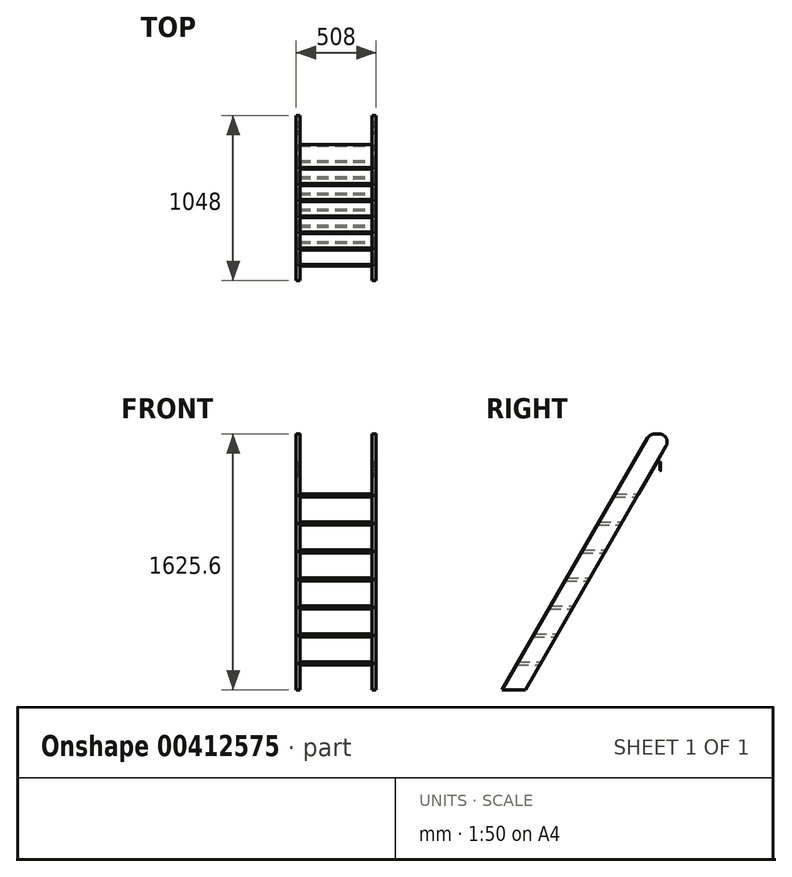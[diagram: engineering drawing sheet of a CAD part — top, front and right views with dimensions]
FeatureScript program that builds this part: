
annotation { "Feature Type Name" : "Feature", "Feature Type Description" : "" }
export const myFeature = defineFeature(function(context is Context, id is Id, definition is map)
    precondition{}
    {
        {
            var Q0;
            Q0=qCreatedBy(makeId("Right.planeOp"),FACE);
            var sketch = newSketch(context, id + "F0", { "sketchPlane" : qUnion([Q0])});
            skLineSegment(sketch, "E0", {"start": v(-87.99, 0) * mm, "end": v(-117.32, 0) * mm});
            skLineSegment(sketch, "E1", {"start": v(-161.31, -25.4) * mm, "end": v(-1085.19, -1625.6) * mm});
            skLineSegment(sketch, "E2", {"start": v(-1085.19, -1625.6) * mm, "end": v(-938.54, -1625.6) * mm});
            skLineSegment(sketch, "E3", {"start": v(-938.54, -1625.6) * mm, "end": v(-154.37, -267.38) * mm});
            skLineSegment(sketch, "E4", {"start": v(-982.53, -1447.8) * mm, "end": v(-835.89, -1447.8) * mm});
            skLineSegment(sketch, "E5", {"start": v(-879.88, -1270) * mm, "end": v(-733.23, -1270) * mm});
            skLineSegment(sketch, "E6", {"start": v(-777.23, -1092.2) * mm, "end": v(-630.58, -1092.2) * mm});
            skLineSegment(sketch, "E7", {"start": v(-674.58, -914.4) * mm, "end": v(-527.93, -914.4) * mm});
            skLineSegment(sketch, "E8", {"start": v(-571.92, -736.6) * mm, "end": v(-425.28, -736.6) * mm});
            skLineSegment(sketch, "E9.0", {"start": v(-993.53, -1466.85) * mm, "end": v(-846.89, -1466.85) * mm});
            skLineSegment(sketch, "E10.0", {"start": v(-890.88, -1289.05) * mm, "end": v(-744.23, -1289.05) * mm});
            skLineSegment(sketch, "E11.0", {"start": v(-788.23, -1111.25) * mm, "end": v(-641.58, -1111.25) * mm});
            skLineSegment(sketch, "E12.0", {"start": v(-685.57, -933.45) * mm, "end": v(-538.93, -933.45) * mm});
            skLineSegment(sketch, "E13.0", {"start": v(-582.92, -755.65) * mm, "end": v(-436.27, -755.65) * mm});
            skLineSegment(sketch, "E14.0", {"start": v(-469.27, -558.8) * mm, "end": v(-322.62, -558.8) * mm});
            skLineSegment(sketch, "E15.0", {"start": v(-480.27, -577.85) * mm, "end": v(-333.62, -577.85) * mm});
            skLineSegment(sketch, "E16.0", {"start": v(-366.62, -381) * mm, "end": v(-219.97, -381) * mm});
            skLineSegment(sketch, "E17.0", {"start": v(-377.62, -400.05) * mm, "end": v(-230.97, -400.05) * mm});
            skArc(sketch, "E18.filletArc", {"start": v(-117.32, 0) * mm, "mid": v(-142.72, -6.8) * mm, "end": v(-161.31, -25.4) * mm});
            skPoint(sketch, "E19.visualSharp", {"position": v(0, 0) * mm});
            skArc(sketch, "E19.filletArc", {"start": v(-44, -76.2) * mm, "mid": v(-44, -25.4) * mm, "end": v(-87.99, 0) * mm});
            skLineSegment(sketch, "E20", {"start": v(-78.6, -180.98) * mm, "end": v(-78.6, -231.78) * mm});
            skLineSegment(sketch, "E21", {"start": v(-78.6, -231.78) * mm, "end": v(-81.77, -231.78) * mm});
            skLineSegment(sketch, "E22", {"start": v(-81.77, -231.78) * mm, "end": v(-81.77, -184.15) * mm});
            skLineSegment(sketch, "E23", {"start": v(-81.77, -177.8) * mm, "end": v(-102.65, -177.8) * mm});
            skLineSegment(sketch, "E24.trimOffspring", {"start": v(-154.37, -267.38) * mm, "end": v(-44, -76.2) * mm});
            skLineSegment(sketch, "E25.0", {"start": v(-84.94, -180.98) * mm, "end": v(-100.82, -180.98) * mm});
            skPoint(sketch, "E26.visualSharp", {"position": v(-100.82, -180.98) * mm});
            skPoint(sketch, "E27.visualSharp", {"position": v(-81.77, -180.98) * mm});
            skArc(sketch, "E27.filletArc", {"start": v(-81.77, -184.15) * mm, "mid": v(-82.7, -181.9) * mm, "end": v(-84.94, -180.98) * mm});
            skPoint(sketch, "E28.visualSharp", {"position": v(-78.6, -177.8) * mm});
            skArc(sketch, "E28.filletArc", {"start": v(-78.6, -180.98) * mm, "mid": v(-79.52, -178.73) * mm, "end": v(-81.77, -177.8) * mm});
            skPoint(sketch, "E29.visualSharp", {"position": v(-102.65, -177.8) * mm});
            skLineSegment(sketch, "E30", {"start": v(-102.65, -177.8) * mm, "end": v(-154.37, -267.38) * mm});
            skLineSegment(sketch, "E31", {"start": v(-154.37, -267.38) * mm, "end": v(-151.62, -268.96) * mm});
            skLineSegment(sketch, "E32", {"start": v(-151.62, -268.96) * mm, "end": v(-100.82, -180.98) * mm});
            skSolve(sketch);
        }
        {
            var Q0;
            Q0=makeQuery(id+"F0.imprint","IMPRINT",FACE,{"disambiguationData":[TD([[makeQuery(id+"F0.imprint","IMPRINT",EDGE,{"derivedFrom":sQuery(id+"F0.wireOp",EDGE,"E0")}),1.0]])]});
            var Q1;
            {var subQ0=sQuery(id+"F0.wireOp",EDGE,"E16.0");Q1=makeQuery(id+"F0.imprint","IMPRINT",FACE,{"disambiguationData":[TD([[makeQuery(id+"F0.imprint","IMPRINT",EDGE,{"derivedFrom":subQ0}),-1.0]])]});}
            var Q2;
            {var subQ0=sQuery(id+"F0.wireOp",EDGE,"E14.0");Q2=makeQuery(id+"F0.imprint","IMPRINT",FACE,{"disambiguationData":[TD([[makeQuery(id+"F0.imprint","IMPRINT",EDGE,{"derivedFrom":subQ0}),1.0]])]});}
            var Q3;
            {var subQ0=sQuery(id+"F0.wireOp",EDGE,"E14.0");Q3=makeQuery(id+"F0.imprint","IMPRINT",FACE,{"disambiguationData":[TD([[makeQuery(id+"F0.imprint","IMPRINT",EDGE,{"derivedFrom":subQ0}),-1.0]])]});}
            var Q4;
            {var subQ0=sQuery(id+"F0.wireOp",EDGE,"E8");Q4=makeQuery(id+"F0.imprint","IMPRINT",FACE,{"disambiguationData":[TD([[makeQuery(id+"F0.imprint","IMPRINT",EDGE,{"derivedFrom":subQ0}),1.0]])]});}
            var Q5;
            {var subQ0=sQuery(id+"F0.wireOp",EDGE,"E8");Q5=makeQuery(id+"F0.imprint","IMPRINT",FACE,{"disambiguationData":[TD([[makeQuery(id+"F0.imprint","IMPRINT",EDGE,{"derivedFrom":subQ0}),-1.0]])]});}
            var Q6;
            {var subQ0=sQuery(id+"F0.wireOp",EDGE,"E7");Q6=makeQuery(id+"F0.imprint","IMPRINT",FACE,{"disambiguationData":[TD([[makeQuery(id+"F0.imprint","IMPRINT",EDGE,{"derivedFrom":subQ0}),1.0]])]});}
            var Q7;
            {var subQ0=sQuery(id+"F0.wireOp",EDGE,"E6");Q7=makeQuery(id+"F0.imprint","IMPRINT",FACE,{"disambiguationData":[TD([[makeQuery(id+"F0.imprint","IMPRINT",EDGE,{"derivedFrom":subQ0}),1.0]])]});}
            var Q8;
            {var subQ0=sQuery(id+"F0.wireOp",EDGE,"E5");Q8=makeQuery(id+"F0.imprint","IMPRINT",FACE,{"disambiguationData":[TD([[makeQuery(id+"F0.imprint","IMPRINT",EDGE,{"derivedFrom":subQ0}),1.0]])]});}
            var Q9;
            {var subQ0=sQuery(id+"F0.wireOp",EDGE,"E4");Q9=makeQuery(id+"F0.imprint","IMPRINT",FACE,{"disambiguationData":[TD([[makeQuery(id+"F0.imprint","IMPRINT",EDGE,{"derivedFrom":subQ0}),1.0]])]});}
            var Q10;
            {var subQ0=sQuery(id+"F0.wireOp",EDGE,"E2");Q10=makeQuery(id+"F0.imprint","IMPRINT",FACE,{"disambiguationData":[TD([[makeQuery(id+"F0.imprint","IMPRINT",EDGE,{"derivedFrom":subQ0}),1.0]])]});}
            var Q11;
            {var subQ0=sQuery(id+"F0.wireOp",EDGE,"E4");Q11=makeQuery(id+"F0.imprint","IMPRINT",FACE,{"disambiguationData":[TD([[makeQuery(id+"F0.imprint","IMPRINT",EDGE,{"derivedFrom":subQ0}),-1.0]])]});}
            var Q12;
            {var subQ0=sQuery(id+"F0.wireOp",EDGE,"E5");Q12=makeQuery(id+"F0.imprint","IMPRINT",FACE,{"disambiguationData":[TD([[makeQuery(id+"F0.imprint","IMPRINT",EDGE,{"derivedFrom":subQ0}),-1.0]])]});}
            var Q13;
            {var subQ0=sQuery(id+"F0.wireOp",EDGE,"E6");Q13=makeQuery(id+"F0.imprint","IMPRINT",FACE,{"disambiguationData":[TD([[makeQuery(id+"F0.imprint","IMPRINT",EDGE,{"derivedFrom":subQ0}),-1.0]])]});}
            var Q14;
            {var subQ0=sQuery(id+"F0.wireOp",EDGE,"E7");Q14=makeQuery(id+"F0.imprint","IMPRINT",FACE,{"disambiguationData":[TD([[makeQuery(id+"F0.imprint","IMPRINT",EDGE,{"derivedFrom":subQ0}),-1.0]])]});}
            var Q15;
            {var subQ0=sQuery(id+"F0.wireOp",EDGE,"B96Wzpzp-lwjt-oDgw-DfDW-PDG2NPqT7k9v");Q15=makeQuery(id+"F0.imprint","IMPRINT",FACE,{"disambiguationData":[TD([[makeQuery(id+"F0.imprint","IMPRINT",EDGE,{"derivedFrom":subQ0}),-1.0]])]});}
            extrude(context, id + "F1", {"entities" : qUnion([Q0, Q1, Q2, Q3, Q4, Q5, Q6, Q7, Q8, Q9, Q10, Q11, Q12, Q13, Q14, Q15]), "depth" : 25.4 * mm});
        }
        {
            var Q0;
            {var subQ0=sQuery(id+"F0.wireOp",EDGE,"E16.0");Q0=makeQuery(id+"F0.imprint","IMPRINT",FACE,{"disambiguationData":[TD([[makeQuery(id+"F0.imprint","IMPRINT",EDGE,{"derivedFrom":subQ0}),-1.0]])]});}
            var Q1;
            {var subQ0=sQuery(id+"F0.wireOp",EDGE,"E14.0");Q1=makeQuery(id+"F0.imprint","IMPRINT",FACE,{"disambiguationData":[TD([[makeQuery(id+"F0.imprint","IMPRINT",EDGE,{"derivedFrom":subQ0}),-1.0]])]});}
            var Q2;
            {var subQ0=sQuery(id+"F0.wireOp",EDGE,"E8");Q2=makeQuery(id+"F0.imprint","IMPRINT",FACE,{"disambiguationData":[TD([[makeQuery(id+"F0.imprint","IMPRINT",EDGE,{"derivedFrom":subQ0}),-1.0]])]});}
            var Q3;
            {var subQ0=sQuery(id+"F0.wireOp",EDGE,"E7");Q3=makeQuery(id+"F0.imprint","IMPRINT",FACE,{"disambiguationData":[TD([[makeQuery(id+"F0.imprint","IMPRINT",EDGE,{"derivedFrom":subQ0}),-1.0]])]});}
            var Q4;
            {var subQ0=sQuery(id+"F0.wireOp",EDGE,"E6");Q4=makeQuery(id+"F0.imprint","IMPRINT",FACE,{"disambiguationData":[TD([[makeQuery(id+"F0.imprint","IMPRINT",EDGE,{"derivedFrom":subQ0}),-1.0]])]});}
            var Q5;
            {var subQ0=sQuery(id+"F0.wireOp",EDGE,"E5");Q5=makeQuery(id+"F0.imprint","IMPRINT",FACE,{"disambiguationData":[TD([[makeQuery(id+"F0.imprint","IMPRINT",EDGE,{"derivedFrom":subQ0}),-1.0]])]});}
            var Q6;
            {var subQ0=sQuery(id+"F0.wireOp",EDGE,"E4");Q6=makeQuery(id+"F0.imprint","IMPRINT",FACE,{"disambiguationData":[TD([[makeQuery(id+"F0.imprint","IMPRINT",EDGE,{"derivedFrom":subQ0}),-1.0]])]});}
            extrude(context, id + "F2", {"entities" : qUnion([Q0, Q1, Q2, Q3, Q4, Q5, Q6]), "operationType" : NewBodyOperationType.REMOVE, "depth" : 9.52 * mm});
        }
        {
            var Q0;
            Q0=makeQuery(id+"F0.imprint","IMPRINT",FACE,{"disambiguationData":[TD([[makeQuery(id+"F0.imprint","IMPRINT",EDGE,{"derivedFrom":sQuery(id+"F0.wireOp",EDGE,"E20")}),-1.0]])]});
            extrude(context, id + "F3", {"entities" : qUnion([Q0]), "depth" : 25.4 * mm});
        }
        {
            var Q0;
            Q0=qCreatedBy(makeId("Right.planeOp"),FACE);
            cPlane(context, id + "F4", {"entities" : qUnion([Q0]), "cplaneType" : CPlaneType.OFFSET, "offset" : 228.6 * mm, "oppositeDirection" : true, "width" : 152.4 * mm, "height" : 152.4 * mm});
        }
        {
            var Q0;
            Q0=makeQuery(id+"F1.opExtrude","SWEPT_BODY",BODY,{"disambiguationData":[OSD([sQuery(id+"F0.wireOp",EDGE,"E0"),sQuery(id+"F0.wireOp",EDGE,"E1"),sQuery(id+"F0.wireOp",EDGE,"E2"),sQuery(id+"F0.wireOp",EDGE,"E3"),sQuery(id+"F0.wireOp",EDGE,"E18.filletArc"),sQuery(id+"F0.wireOp",EDGE,"E19.filletArc"),sQuery(id+"F0.wireOp",EDGE,"87bb9fc3-04ee-44ed-8673-97e675bece17.0"),sQuery(id+"F0.wireOp",EDGE,"B96Wzpzp-lwjt-oDgw-DfDW-PDG2NPqT7k9v"),sQuery(id+"F0.wireOp",EDGE,"E24.trimOffspring")])]});
            var Q1;
            Q1=qCreatedBy(id+"F4.planeOp",FACE);
            mirror(context, id + "F5", {"entities" : qUnion([Q0]), "mirrorPlane" : qUnion([Q1])});
        }
        {
            var Q0;
            Q0=makeQuery(id+"F2.boolean.opBoolean","COPY",FACE,{"derivedFrom":makeQuery(id+"F2.opExtrude","CAP_FACE",FACE,{"disambiguationData":[OSD([sQuery(id+"F0.wireOp",EDGE,"E1"),sQuery(id+"F0.wireOp",EDGE,"E3"),sQuery(id+"F0.wireOp",EDGE,"E16.0"),sQuery(id+"F0.wireOp",EDGE,"E17.0")])],"isStart":false})});
            var Q1;
            Q1=makeQuery(id+"F2.boolean.opBoolean","COPY",FACE,{"derivedFrom":makeQuery(id+"F2.opExtrude","CAP_FACE",FACE,{"disambiguationData":[OSD([sQuery(id+"F0.wireOp",EDGE,"E1"),sQuery(id+"F0.wireOp",EDGE,"E3"),sQuery(id+"F0.wireOp",EDGE,"E14.0"),sQuery(id+"F0.wireOp",EDGE,"E15.0")])],"isStart":false})});
            var Q2;
            Q2=makeQuery(id+"F2.boolean.opBoolean","COPY",FACE,{"derivedFrom":makeQuery(id+"F2.opExtrude","CAP_FACE",FACE,{"disambiguationData":[OSD([sQuery(id+"F0.wireOp",EDGE,"E1"),sQuery(id+"F0.wireOp",EDGE,"E3"),sQuery(id+"F0.wireOp",EDGE,"E8"),sQuery(id+"F0.wireOp",EDGE,"E13.0")])],"isStart":false})});
            var Q3;
            Q3=makeQuery(id+"F2.boolean.opBoolean","COPY",FACE,{"derivedFrom":makeQuery(id+"F2.opExtrude","CAP_FACE",FACE,{"disambiguationData":[OSD([sQuery(id+"F0.wireOp",EDGE,"E1"),sQuery(id+"F0.wireOp",EDGE,"E3"),sQuery(id+"F0.wireOp",EDGE,"E7"),sQuery(id+"F0.wireOp",EDGE,"E12.0")])],"isStart":false})});
            var Q4;
            Q4=makeQuery(id+"F2.boolean.opBoolean","COPY",FACE,{"derivedFrom":makeQuery(id+"F2.opExtrude","CAP_FACE",FACE,{"disambiguationData":[OSD([sQuery(id+"F0.wireOp",EDGE,"E1"),sQuery(id+"F0.wireOp",EDGE,"E3"),sQuery(id+"F0.wireOp",EDGE,"E6"),sQuery(id+"F0.wireOp",EDGE,"E11.0")])],"isStart":false})});
            var Q5;
            Q5=makeQuery(id+"F2.boolean.opBoolean","COPY",FACE,{"derivedFrom":makeQuery(id+"F2.opExtrude","CAP_FACE",FACE,{"disambiguationData":[OSD([sQuery(id+"F0.wireOp",EDGE,"E1"),sQuery(id+"F0.wireOp",EDGE,"E3"),sQuery(id+"F0.wireOp",EDGE,"E5"),sQuery(id+"F0.wireOp",EDGE,"E10.0")])],"isStart":false})});
            var Q6;
            Q6=makeQuery(id+"F2.boolean.opBoolean","COPY",FACE,{"derivedFrom":makeQuery(id+"F2.opExtrude","CAP_FACE",FACE,{"disambiguationData":[OSD([sQuery(id+"F0.wireOp",EDGE,"E1"),sQuery(id+"F0.wireOp",EDGE,"E3"),sQuery(id+"F0.wireOp",EDGE,"E4"),sQuery(id+"F0.wireOp",EDGE,"E9.0")])],"isStart":false})});
            extrude(context, id + "F6", {"entities" : qUnion([Q0, Q1, Q2, Q3, Q4, Q5, Q6]), "endBound" : BoundingType.UP_TO_NEXT, "depth" : 457.2 * mm});
        }
        {
            var Q0;
            Q0=makeQuery(id+"F3.opExtrude","SWEPT_FACE",FACE,{"disambiguationData":[OSD([sQuery(id+"F0.wireOp",EDGE,"E32")])]});
            var sketch = newSketch(context, id + "F7", { "sketchPlane" : qUnion([Q0])});
            skPoint(sketch, "E33", {"position": v(-12.7, -219.84) * mm});
            skPoint(sketch, "E34", {"position": v(-12.7, -289.69) * mm});
            skSolve(sketch);
        }
        {
            var Q0;
            Q0=sQuery(id+"F7.wireOp",VERTEX,"E33");
            var Q1;
            Q1=sQuery(id+"F7.wireOp",VERTEX,"E34");
            var Q2;
            Q2=makeQuery(id+"F3.opExtrude","SWEPT_BODY",BODY,{"disambiguationData":[OSD([sQuery(id+"F0.wireOp",EDGE,"E20"),sQuery(id+"F0.wireOp",EDGE,"E21"),sQuery(id+"F0.wireOp",EDGE,"E22"),sQuery(id+"F0.wireOp",EDGE,"E23"),sQuery(id+"F0.wireOp",EDGE,"87bb9fc3-04ee-44ed-8673-97e675bece17.0"),sQuery(id+"F0.wireOp",EDGE,"a5deaf5e-a050-4f96-910e-6dbd6f1f3d3d.0"),sQuery(id+"F0.wireOp",EDGE,"E25.0"),sQuery(id+"F0.wireOp",EDGE,"E26.filletArc"),sQuery(id+"F0.wireOp",EDGE,"E27.filletArc"),sQuery(id+"F0.wireOp",EDGE,"E28.filletArc"),sQuery(id+"F0.wireOp",EDGE,"i6ceQ2OO-8qjx-83eS-yppq-eLtZrgpOSD01"),sQuery(id+"F0.wireOp",EDGE,"E29.filletArc")])]});
            hole(context, id + "F8", {"style" : HoleStyle.C_SINK, "endStyle" : HoleEndStyle.THROUGH, "standardTappedOrClearance" : lookupTablePath({ "standard" : "ANSI", "fit" : "Normal (ASME)", "size" : "#8", "type" : "Clearance" }), "standardBlindInLast" : lookupTablePath({ "fit" : "Free", "standard" : "ANSI", "size" : "#8", "type" : "Clearance" }), "holeDiameter" : 4.5 * mm, "cSinkDiameter" : 9.12 * mm, "cSinkAngle" : 82 * degree, "isTappedThrough" : true, "tappedDepth" : 12.7 * mm, "tapClearance" : 3, "locations" : qUnion([Q0, Q1]), "scope" : qUnion([Q2])});
        }
        {
            var Q0;
            {var subQ0=sQuery(id+"F0.wireOp",EDGE,"E32");Q0=makeQuery(id+"F7.imprint","IMPRINT",FACE,{"disambiguationData":[TD([[makeQuery(id+"F7.imprint","IMPRINT",EDGE,{"derivedFrom":makeQuery(id+"F3.opExtrude","CAP_EDGE",EDGE,{"disambiguationData":[OSD([subQ0])],"isStart":true})}),1.0]])]});}
            cPlane(context, id + "F9", {"entities" : qUnion([Q0]), "cplaneType" : CPlaneType.OFFSET, "offset" : 50.8 * mm, "width" : 152.4 * mm, "height" : 152.4 * mm});
        }
        {
            var Q0;
            Q0=qCreatedBy(id+"F9.planeOp",FACE);
            var sketch = newSketch(context, id + "F10", { "sketchPlane" : qUnion([Q0])});
            skPoint(sketch, "E35", {"position": v(-12.7, -219.84) * mm});
            skSolve(sketch);
        }
        {
            var Q0;
            Q0=sQuery(id+"F10.wireOp",VERTEX,"E35");
            var Q1;
            Q1=makeQuery(id+"F3.opExtrude","SWEPT_BODY",BODY,{"disambiguationData":[OSD([sQuery(id+"F0.wireOp",EDGE,"E20"),sQuery(id+"F0.wireOp",EDGE,"E21"),sQuery(id+"F0.wireOp",EDGE,"E22"),sQuery(id+"F0.wireOp",EDGE,"E23"),sQuery(id+"F0.wireOp",EDGE,"87bb9fc3-04ee-44ed-8673-97e675bece17.0"),sQuery(id+"F0.wireOp",EDGE,"a5deaf5e-a050-4f96-910e-6dbd6f1f3d3d.0"),sQuery(id+"F0.wireOp",EDGE,"E25.0"),sQuery(id+"F0.wireOp",EDGE,"E26.filletArc"),sQuery(id+"F0.wireOp",EDGE,"E27.filletArc"),sQuery(id+"F0.wireOp",EDGE,"E28.filletArc"),sQuery(id+"F0.wireOp",EDGE,"i6ceQ2OO-8qjx-83eS-yppq-eLtZrgpOSD01"),sQuery(id+"F0.wireOp",EDGE,"E29.filletArc")])]});
            hole(context, id + "F11", {"style" : HoleStyle.SIMPLE, "endStyle" : HoleEndStyle.BLIND, "standardTappedOrClearance" : lookupTablePath({ "standard" : "ANSI", "fit" : "Normal (ASME)", "size" : "3/8", "type" : "Clearance" }), "standardBlindInLast" : lookupTablePath({ "fit" : "Free", "standard" : "ANSI", "size" : "3/8", "type" : "Clearance" }), "holeDiameter" : 10.08 * mm, "holeDepth" : 6.35 * mm, "isTappedThrough" : true, "tappedDepth" : 12.7 * mm, "tapClearance" : 3, "locations" : qUnion([Q0]), "scope" : qUnion([Q1])});
        }
        {
            var Q0;
            Q0=makeQuery(id+"F3.opExtrude","CAP_EDGE",EDGE,{"disambiguationData":[OSD([sQuery(id+"F0.wireOp",EDGE,"E21")])],"isStart":false});
            var Q1;
            Q1=makeQuery(id+"F3.opExtrude","CAP_EDGE",EDGE,{"disambiguationData":[OSD([sQuery(id+"F0.wireOp",EDGE,"E21")])],"isStart":true});
            fillet(context, id + "F12", {"entities" : qUnion([Q0, Q1]), "radius" : 3.17 * mm, "tangentPropagation" : true, "allowEdgeOverflow" : false});
        }
        {
            var Q0;
            Q0=makeQuery(id+"F3.opExtrude","SWEPT_BODY",BODY,{"disambiguationData":[OSD([sQuery(id+"F0.wireOp",EDGE,"E20"),sQuery(id+"F0.wireOp",EDGE,"E21"),sQuery(id+"F0.wireOp",EDGE,"E22"),sQuery(id+"F0.wireOp",EDGE,"E23"),sQuery(id+"F0.wireOp",EDGE,"87bb9fc3-04ee-44ed-8673-97e675bece17.0"),sQuery(id+"F0.wireOp",EDGE,"a5deaf5e-a050-4f96-910e-6dbd6f1f3d3d.0"),sQuery(id+"F0.wireOp",EDGE,"E25.0"),sQuery(id+"F0.wireOp",EDGE,"E26.filletArc"),sQuery(id+"F0.wireOp",EDGE,"E27.filletArc"),sQuery(id+"F0.wireOp",EDGE,"E28.filletArc"),sQuery(id+"F0.wireOp",EDGE,"i6ceQ2OO-8qjx-83eS-yppq-eLtZrgpOSD01"),sQuery(id+"F0.wireOp",EDGE,"E29.filletArc")])]});
            var Q1;
            Q1=qCreatedBy(id+"F4.planeOp",FACE);
            mirror(context, id + "F13", {"entities" : qUnion([Q0]), "mirrorPlane" : qUnion([Q1])});
        }
    });
